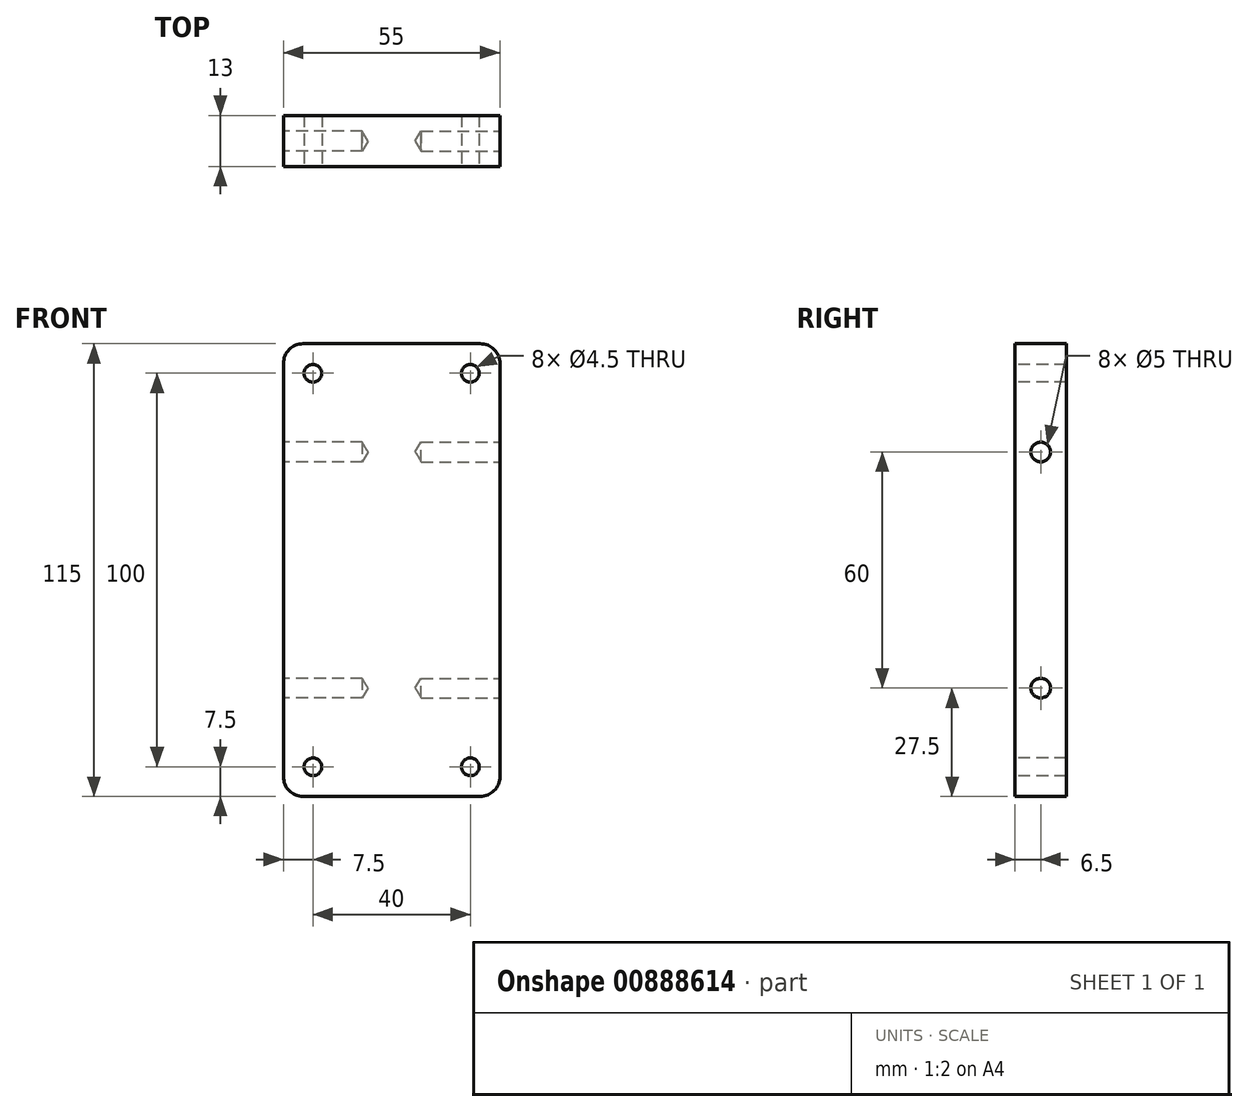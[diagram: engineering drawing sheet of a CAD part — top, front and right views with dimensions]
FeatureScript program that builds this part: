
annotation { "Feature Type Name" : "Feature", "Feature Type Description" : "" }
export const myFeature = defineFeature(function(context is Context, id is Id, definition is map)
    precondition{}
    {
        {
            var Q0;
            Q0=qCreatedBy(makeId("Front.planeOp"),FACE);
            var sketch = newSketch(context, id + "F0", { "sketchPlane" : qUnion([Q0])});
            skLineSegment(sketch, "E0.bottom", {"start": v(27.5, 57.5) * mm, "end": v(-27.5, 57.5) * mm});
            skLineSegment(sketch, "E0.top", {"start": v(27.5, -57.5) * mm, "end": v(-27.5, -57.5) * mm});
            skLineSegment(sketch, "E0.left", {"start": v(27.5, 57.5) * mm, "end": v(27.5, -57.5) * mm});
            skLineSegment(sketch, "E0.right", {"start": v(-27.5, 57.5) * mm, "end": v(-27.5, -57.5) * mm});
            skPoint(sketch, "E0.middle", {"position": v(0, 0) * mm});
            skSolve(sketch);
        }
        {
            var Q0;
            Q0=makeQuery(id+"F0.imprint","IMPRINT",FACE,{"disambiguationData":[TD([[makeQuery(id+"F0.imprint","IMPRINT",EDGE,{"derivedFrom":sQuery(id+"F0.wireOp",EDGE,"E0.bottom")}),1.0]])]});
            extrude(context, id + "F1", {"entities" : qUnion([Q0]), "depth" : 13 * mm, "offsetDistance" : 25 * mm});
        }
        {
            var Q0;
            Q0=makeQuery(id+"F1.opExtrude","CAP_FACE",FACE,{"disambiguationData":[OSD([sQuery(id+"F0.wireOp",EDGE,"E0.bottom"),sQuery(id+"F0.wireOp",EDGE,"E0.top"),sQuery(id+"F0.wireOp",EDGE,"E0.left"),sQuery(id+"F0.wireOp",EDGE,"E0.right")])],"isStart":false});
            var sketch = newSketch(context, id + "F2", { "sketchPlane" : qUnion([Q0])});
            skLineSegment(sketch, "E1.bottom", {"start": v(20, 50) * mm, "end": v(-20, 50) * mm, "construction": true});
            skLineSegment(sketch, "E1.top", {"start": v(20, -50) * mm, "end": v(-20, -50) * mm, "construction": true});
            skLineSegment(sketch, "E1.left", {"start": v(20, 50) * mm, "end": v(20, -50) * mm, "construction": true});
            skLineSegment(sketch, "E1.right", {"start": v(-20, 50) * mm, "end": v(-20, -50) * mm, "construction": true});
            skPoint(sketch, "E1.middle", {"position": v(0, 0) * mm});
            skSolve(sketch);
        }
        {
            var Q0;
            Q0=sQuery(id+"F2.wireOp",VERTEX,"E1.bottom.end");
            var Q1;
            Q1=sQuery(id+"F2.wireOp",VERTEX,"E1.bottom.start");
            var Q2;
            Q2=sQuery(id+"F2.wireOp",VERTEX,"E1.top.start");
            var Q3;
            Q3=sQuery(id+"F2.wireOp",VERTEX,"E1.top.end");
            var Q4;
            Q4=makeQuery(id+"F1.opExtrude","SWEPT_BODY",BODY,{"disambiguationData":[OSD([sQuery(id+"F0.wireOp",EDGE,"E0.bottom"),sQuery(id+"F0.wireOp",EDGE,"E0.top"),sQuery(id+"F0.wireOp",EDGE,"E0.left"),sQuery(id+"F0.wireOp",EDGE,"E0.right")])]});
            hole(context, id + "F3", {"style" : HoleStyle.SIMPLE, "endStyle" : HoleEndStyle.BLIND, "holeDiameter" : 4.5 * mm, "majorDiameter" : 5 * mm, "holeDepth" : 30 * mm, "tappedDepth" : 12 * mm, "tapClearance" : 3, "locations" : qUnion([Q0, Q1, Q2, Q3]), "scope" : qUnion([Q4])});
        }
        {
            var Q0;
            Q0=makeQuery(id+"F1.opExtrude","SWEPT_FACE",FACE,{"disambiguationData":[OSD([sQuery(id+"F0.wireOp",EDGE,"E0.left")])]});
            var sketch = newSketch(context, id + "F4", { "sketchPlane" : qUnion([Q0])});
            skCircle(sketch, "E2", {"center": v(-6.5, 30) * mm, "radius": 2.5 * mm});
            skPoint(sketch, "E2.centerSnap0", {"position": v(-6.5, 57.5) * mm});
            skCircle(sketch, "E3", {"center": v(-6.5, -30) * mm, "radius": 2.5 * mm});
            skSolve(sketch);
        }
        {
            var Q0;
            Q0=sQuery(id+"F4.wireOp",VERTEX,"E2.center");
            var Q1;
            Q1=sQuery(id+"F4.wireOp",VERTEX,"E3.center");
            var Q2;
            Q2=makeQuery(id+"F1.opExtrude","SWEPT_BODY",BODY,{"disambiguationData":[OSD([sQuery(id+"F0.wireOp",EDGE,"E0.bottom"),sQuery(id+"F0.wireOp",EDGE,"E0.top"),sQuery(id+"F0.wireOp",EDGE,"E0.left"),sQuery(id+"F0.wireOp",EDGE,"E0.right")])]});
            hole(context, id + "F5", {"style" : HoleStyle.SIMPLE, "endStyle" : HoleEndStyle.BLIND, "holeDiameter" : 5 * mm, "majorDiameter" : 5 * mm, "holeDepth" : 20 * mm, "tappedDepth" : 12 * mm, "tapClearance" : 3, "locations" : qUnion([Q0, Q1]), "scope" : qUnion([Q2])});
        }
        {
            var Q0;
            Q0=makeQuery(id+"F1.opExtrude","SWEPT_FACE",FACE,{"disambiguationData":[OSD([sQuery(id+"F0.wireOp",EDGE,"E0.right")])]});
            var sketch = newSketch(context, id + "F6", { "sketchPlane" : qUnion([Q0])});
            skCircle(sketch, "E4", {"center": v(6.5, 30) * mm, "radius": 2.5 * mm});
            skPoint(sketch, "E4.centerSnap0", {"position": v(6.5, 57.5) * mm});
            skCircle(sketch, "E5", {"center": v(6.5, -30) * mm, "radius": 2.5 * mm});
            skSolve(sketch);
        }
        {
            var Q0;
            Q0=sQuery(id+"F6.wireOp",VERTEX,"E4.center");
            var Q1;
            Q1=sQuery(id+"F6.wireOp",VERTEX,"E5.center");
            var Q2;
            Q2=makeQuery(id+"F1.opExtrude","SWEPT_BODY",BODY,{"disambiguationData":[OSD([sQuery(id+"F0.wireOp",EDGE,"E0.bottom"),sQuery(id+"F0.wireOp",EDGE,"E0.top"),sQuery(id+"F0.wireOp",EDGE,"E0.left"),sQuery(id+"F0.wireOp",EDGE,"E0.right")])]});
            hole(context, id + "F7", {"style" : HoleStyle.SIMPLE, "endStyle" : HoleEndStyle.BLIND, "holeDiameter" : 5 * mm, "majorDiameter" : 5 * mm, "holeDepth" : 20 * mm, "tappedDepth" : 12 * mm, "tapClearance" : 3, "locations" : qUnion([Q0, Q1]), "scope" : qUnion([Q2])});
        }
        {
            var Q0;
            Q0=makeQuery(id+"F1.opExtrude","SWEPT_EDGE",EDGE,{"disambiguationData":[OSD([sQuery(id+"F0.wireOp",EDGE,"E0.bottom"),sQuery(id+"F0.wireOp",EDGE,"E0.left")])]});
            var Q1;
            Q1=makeQuery(id+"F1.opExtrude","SWEPT_EDGE",EDGE,{"disambiguationData":[OSD([sQuery(id+"F0.wireOp",EDGE,"E0.bottom"),sQuery(id+"F0.wireOp",EDGE,"E0.right")])]});
            var Q2;
            Q2=makeQuery(id+"F1.opExtrude","SWEPT_EDGE",EDGE,{"disambiguationData":[OSD([sQuery(id+"F0.wireOp",EDGE,"E0.top"),sQuery(id+"F0.wireOp",EDGE,"E0.right")])]});
            var Q3;
            Q3=makeQuery(id+"F1.opExtrude","SWEPT_EDGE",EDGE,{"disambiguationData":[OSD([sQuery(id+"F0.wireOp",EDGE,"E0.top"),sQuery(id+"F0.wireOp",EDGE,"E0.left")])]});
            fillet(context, id + "F8", {"entities" : qUnion([Q0, Q1, Q2, Q3]), "tangentPropagation" : true, "radius" : 5 * mm, "defaultsChanged" : false, "vertexSettings" : [], "allowEdgeOverflow" : false});
        }
    });
